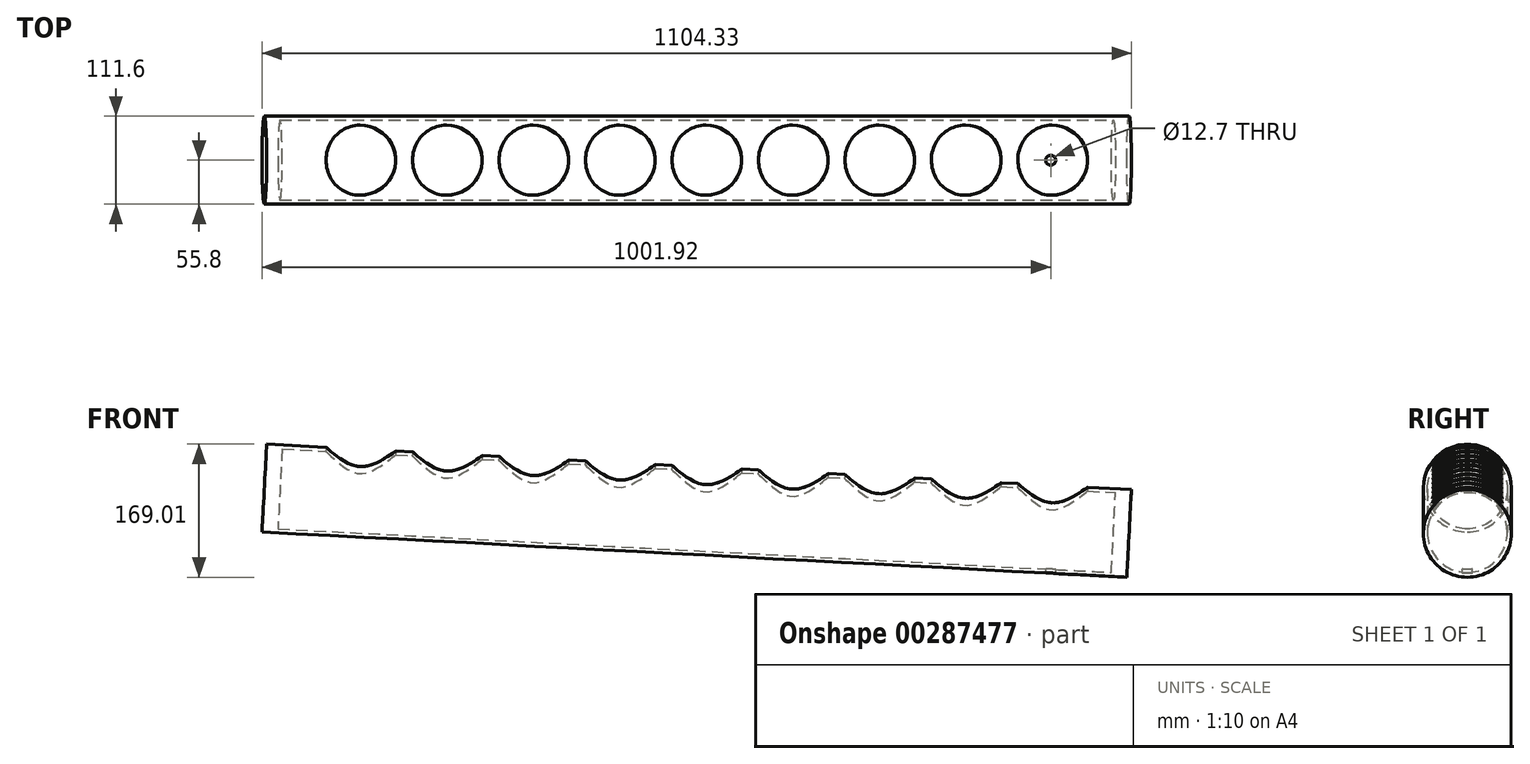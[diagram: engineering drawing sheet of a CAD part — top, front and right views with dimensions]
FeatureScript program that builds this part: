
annotation { "Feature Type Name" : "Feature", "Feature Type Description" : "" }
export const myFeature = defineFeature(function(context is Context, id is Id, definition is map)
    precondition{}
    {
        {
            var Q0;
            Q0=qCreatedBy(makeId("Right.planeOp"),FACE);
            var sketch = newSketch(context, id + "F0", { "sketchPlane" : qUnion([Q0])});
            skCircle(sketch, "E0", {"center": v(0, 0) * mm, "radius": 50.8 * mm});
            skCircle(sketch, "E1.0", {"center": v(0, 0) * mm, "radius": 55.8 * mm});
            skLineSegment(sketch, "E2", {"start": v(-50.8, 0) * mm, "end": v(50.8, 0) * mm, "construction": true});
            skSolve(sketch);
        }
        {
            var Q0;
            Q0=qSketchRegion(id+"F0",true);
            extrude(context, id + "F1", {"entities" : qUnion([Q0]), "oppositeDirection" : true, "depth" : 1100 * mm});
        }
        {
            var Q0;
            Q0=qCreatedBy(makeId("Right.planeOp"),FACE);
            var sketch = newSketch(context, id + "F2", { "sketchPlane" : qUnion([Q0])});
            skLineSegment(sketch, "E3", {"start": v(-70.21, 0) * mm, "end": v(69.9, 0) * mm, "construction": true});
            skSolve(sketch);
        }
        {
            var Q0;
            Q0=qCreatedBy(makeId("Top.planeOp"),FACE);
            var sketch = newSketch(context, id + "F3", { "sketchPlane" : qUnion([Q0])});
            skCircle(sketch, "E4", {"center": v(-100, 0) * mm, "radius": 44.45 * mm});
            skCircle(sketch, "E5.1.0.0", {"center": v(-210, 0) * mm, "radius": 44.45 * mm});
            skCircle(sketch, "E5.2.0.0", {"center": v(-320, 0) * mm, "radius": 44.45 * mm});
            skCircle(sketch, "E5.3.0.0", {"center": v(-430, 0) * mm, "radius": 44.45 * mm});
            skCircle(sketch, "E5.4.0.0", {"center": v(-540, 0) * mm, "radius": 44.45 * mm});
            skCircle(sketch, "E5.5.0.0", {"center": v(-650, 0) * mm, "radius": 44.45 * mm});
            skCircle(sketch, "E5.6.0.0", {"center": v(-760, 0) * mm, "radius": 44.45 * mm});
            skCircle(sketch, "E5.7.0.0", {"center": v(-870, 0) * mm, "radius": 44.45 * mm});
            skCircle(sketch, "E5.8.0.0", {"center": v(-980, 0) * mm, "radius": 44.45 * mm});
            skLineSegment(sketch, "E5.direction1", {"start": v(-100, 0) * mm, "end": v(-210, 0) * mm, "construction": true});
            skSolve(sketch);
        }
        {
            var Q0;
            Q0=qSketchRegion(id+"F3",true);
            extrude(context, id + "F4", {"entities" : qUnion([Q0]), "operationType" : NewBodyOperationType.REMOVE, "endBound" : BoundingType.THROUGH_ALL, "depth" : 25 * mm});
        }
        {
            var Q0;
            Q0=makeQuery(id+"F1.opExtrude","SWEPT_BODY",BODY,{"disambiguationData":[OSD([sQuery(id+"F0.wireOp",EDGE,"E0"),sQuery(id+"F0.wireOp",EDGE,"E1.0")])]});
            var Q1;
            Q1=sQuery(id+"F2.wireOp",EDGE,"E3");
            transform(context, id + "F5", {"entities" : qUnion([Q0]), "transformType" : TransformType.ROTATION, "transformAxis" : qUnion([Q1]), "angle" : 3 * degree, "makeCopy" : false});
        }
        {
            var Q0;
            Q0=makeQuery(id+"F1.opExtrude","CAP_FACE",FACE,{"disambiguationData":[OSD([sQuery(id+"F0.wireOp",EDGE,"E0"),sQuery(id+"F0.wireOp",EDGE,"E1.0")])],"isStart":true});
            var sketch = newSketch(context, id + "F6", { "sketchPlane" : qUnion([Q0])});
            skCircle(sketch, "E6", {"center": v(0, 0) * mm, "radius": 50.8 * mm});
            skSolve(sketch);
        }
        {
            var Q0;
            Q0=qSketchRegion(id+"F6",true);
            extrude(context, id + "F7", {"entities" : qUnion([Q0]), "operationType" : NewBodyOperationType.ADD, "oppositeDirection" : true, "depth" : 20 * mm});
        }
        {
            var Q0;
            Q0=makeQuery(id+"F1.opExtrude","CAP_FACE",FACE,{"disambiguationData":[OSD([sQuery(id+"F0.wireOp",EDGE,"E0"),sQuery(id+"F0.wireOp",EDGE,"E1.0")])],"isStart":false});
            var sketch = newSketch(context, id + "F8", { "sketchPlane" : qUnion([Q0])});
            skCircle(sketch, "E7", {"center": v(0, 0) * mm, "radius": 53.17 * mm});
            skSolve(sketch);
        }
        {
            var Q0;
            Q0=qSketchRegion(id+"F8",true);
            extrude(context, id + "F9", {"entities" : qUnion([Q0]), "operationType" : NewBodyOperationType.ADD, "oppositeDirection" : true, "depth" : 20 * mm});
        }
        {
            var Q0;
            Q0=qCreatedBy(makeId("Top.planeOp"),FACE);
            var sketch = newSketch(context, id + "F10", { "sketchPlane" : qUnion([Q0])});
            skCircle(sketch, "E8", {"center": v(-99.5, 0) * mm, "radius": 6.35 * mm});
            skSolve(sketch);
        }
        {
            var Q0;
            Q0=qSketchRegion(id+"F10",true);
            extrude(context, id + "F11", {"entities" : qUnion([Q0]), "operationType" : NewBodyOperationType.REMOVE, "endBound" : BoundingType.THROUGH_ALL, "oppositeDirection" : true, "depth" : 25 * mm});
        }
    });
